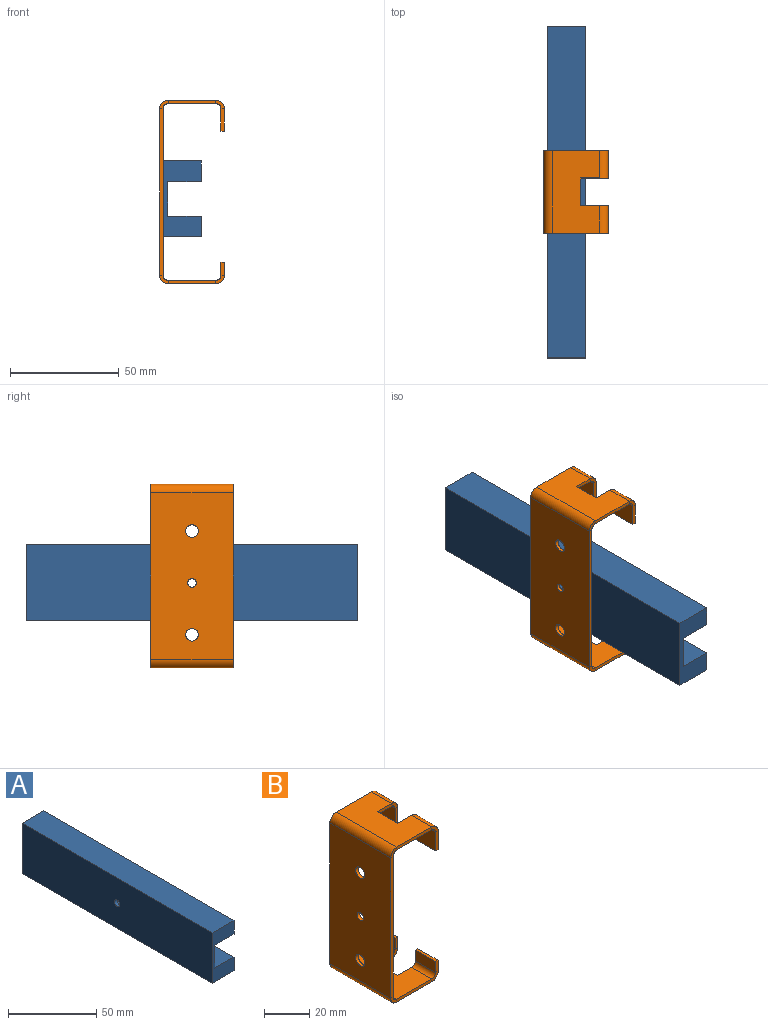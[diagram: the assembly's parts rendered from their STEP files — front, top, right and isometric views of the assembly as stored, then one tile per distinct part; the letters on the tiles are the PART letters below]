
ASSEMBLY  parts=2 mates=1
PART A: 11 faces, bbox 17.5x152.4x34.9 mm
  f0: plane 152.4x34.93mm, normal (-1,0,0), area 5306.7mm2, adj f1,f7,f8,f9,f10
  f1: plane 152.4x17.46mm, normal (0,0,-1), area 2661.3mm2, adj f0,f2,f8,f9
  f2: plane 152.4x9.53mm, normal (1,0,0), area 1451.6mm2, adj f1,f3,f8,f9
  f3: plane 152.4x15.24mm, normal (0,0,1), area 2322.6mm2, adj f2,f4,f8,f9
  f4: plane 152.4x15.88mm, normal (1,0,0), area 2403.5mm2, adj f3,f5,f8,f9,f10
  f5: plane 152.4x15.24mm, normal (0,0,-1), area 2322.6mm2, adj f4,f6,f8,f9
  f6: plane 152.4x9.53mm, normal (1,0,0), area 1451.6mm2, adj f5,f7,f8,f9
  f7: plane 152.4x17.46mm, normal (0,0,1), area 2661.3mm2, adj f0,f6,f8,f9
  f8: plane 34.93x17.46mm, normal (0,-1,0), area 367.9mm2, adj f0,f1,f2,f3,f4,f5,f6,f7
  f9: plane 34.93x17.46mm, normal (0,1,0), area 367.9mm2, adj f0,f1,f2,f3,f4,f5,f6,f7
  f10: cylinder r=2.25mm len=4.5mm, axis (1,0,0), area 31.4mm2, adj f0,f4
PART B: 65 faces, bbox 29.8x38.1x84.3 mm
  f0: plane 22.01x1.59mm, normal (0,-1,0), area 34.9mm2, adj f5,f6,f43,f61
  f1: plane 22.01x1.59mm, normal (0,1,0), area 34.9mm2, adj f5,f6,f44,f53
  f2: plane 8.83x1.59mm, normal (0,-1,0), area 14mm2, adj f3,f5,f6,f52
  f3: plane 12.7x1.59mm, normal (1,0,0), area 20.2mm2, adj f2,f4,f5,f6
  f4: plane 8.83x1.59mm, normal (0,1,0), area 14mm2, adj f3,f5,f6,f62
  f5: plane 38.1x22.01mm, normal (0,0,-1), area 726.5mm2, adj f0,f1,f2,f3,f4,f46,f55,f64
  f6: plane 38.1x22.01mm, normal (0,0,1), area 726.5mm2, adj f0,f1,f2,f3,f4,f45,f54,f63
  f7: plane 76.53x1.59mm, normal (0,1,0), area 121.5mm2, adj f12,f13,f40,f44
  f8: plane 76.53x1.59mm, normal (0,-1,0), area 121.5mm2, adj f12,f13,f39,f43
  f9: cylinder r=2.9mm len=5.79mm, axis (1,0,0), area 28.9mm2, adj f12,f13
  f10: cylinder r=2.9mm len=5.79mm, axis (1,0,0), area 28.9mm2, adj f12,f13
  f11: cylinder r=1.97mm len=3.94mm, axis (1,0,0), area 19.6mm2, adj f12,f13
  f12: plane 76.53x38.1mm, normal (1,0,0), area 2850.9mm2, adj f7,f8,f9,f10,f11,f42,f46
  f13: plane 76.53x38.1mm, normal (-1,0,0), area 2850.9mm2, adj f7,f8,f9,f10,f11,f41,f45
  f14: plane 22.01x1.59mm, normal (0,1,0), area 34.9mm2, adj f19,f20,f27,f40
  f15: plane 22.01x1.59mm, normal (0,-1,0), area 34.9mm2, adj f19,f20,f35,f39
  f16: plane 8.83x1.59mm, normal (0,1,0), area 14mm2, adj f17,f19,f20,f36
  f17: plane 12.7x1.59mm, normal (1,0,0), area 20.2mm2, adj f16,f18,f19,f20
  f18: plane 8.83x1.59mm, normal (0,-1,0), area 14mm2, adj f17,f19,f20,f26
  f19: plane 38.1x22.01mm, normal (0,0,1), area 726.5mm2, adj f14,f15,f16,f17,f18,f29,f38,f42
  f20: plane 38.1x22.01mm, normal (0,0,-1), area 726.5mm2, adj f14,f15,f16,f17,f18,f28,f37,f41
  f21: plane 12.7x1.59mm, normal (0,0,1), area 20.2mm2, adj f22,f23,f24,f25
  f22: plane 5.98x1.59mm, normal (0,1,0), area 9.5mm2, adj f21,f24,f25,f27
  f23: plane 5.98x1.59mm, normal (0,-1,0), area 9.5mm2, adj f21,f24,f25,f26
  f24: plane 12.7x5.98mm, normal (-1,0,0), area 76mm2, adj f21,f22,f23,f29
  f25: plane 12.7x5.98mm, normal (1,0,0), area 76mm2, adj f21,f22,f23,f28
  f26: plane 3.87x3.87mm, normal (0,-1,0), area 7.7mm2, adj f18,f23,f28,f29
  f27: plane 3.87x3.87mm, normal (0,1,0), area 7.7mm2, adj f14,f22,f28,f29
  f28: cylinder r=3.87mm len=12.7mm, axis (0,-1,0), area 77.3mm2, adj f20,f25,f26,f27
  f29: cylinder r=2.29mm len=12.7mm, axis (0,-1,0), area 45.6mm2, adj f19,f24,f26,f27
  f30: plane 5.98x1.59mm, normal (0,-1,0), area 9.5mm2, adj f31,f33,f34,f35
  f31: plane 12.7x1.59mm, normal (0,0,1), area 20.2mm2, adj f30,f32,f33,f34
  f32: plane 5.98x1.59mm, normal (0,1,0), area 9.5mm2, adj f31,f33,f34,f36
  f33: plane 12.7x5.98mm, normal (-1,0,0), area 76mm2, adj f30,f31,f32,f38
  f34: plane 12.7x5.98mm, normal (1,0,0), area 76mm2, adj f30,f31,f32,f37
  f35: plane 3.87x3.87mm, normal (0,-1,0), area 7.7mm2, adj f15,f30,f37,f38
  f36: plane 3.87x3.87mm, normal (0,1,0), area 7.7mm2, adj f16,f32,f37,f38
  f37: cylinder r=3.87mm len=12.7mm, axis (0,-1,0), area 77.3mm2, adj f20,f34,f35,f36
  f38: cylinder r=2.29mm len=12.7mm, axis (0,-1,0), area 45.6mm2, adj f19,f33,f35,f36
  f39: plane 3.87x3.87mm, normal (0,-1,0), area 7.7mm2, adj f8,f15,f41,f42
  f40: plane 3.87x3.87mm, normal (0,1,0), area 7.7mm2, adj f7,f14,f41,f42
  f41: cylinder r=3.87mm len=38.1mm, axis (0,-1,0), area 231.8mm2, adj f13,f20,f39,f40
  f42: cylinder r=2.29mm len=38.1mm, axis (0,-1,0), area 136.8mm2, adj f12,f19,f39,f40
  f43: plane 3.87x3.87mm, normal (0,-1,0), area 7.7mm2, adj f0,f8,f45,f46
  f44: plane 3.87x3.87mm, normal (0,1,0), area 7.7mm2, adj f1,f7,f45,f46
  f45: cylinder r=3.87mm len=38.1mm, axis (0,-1,0), area 231.8mm2, adj f6,f13,f43,f44
  f46: cylinder r=2.29mm len=38.1mm, axis (0,-1,0), area 136.8mm2, adj f5,f12,f43,f44
  f47: plane 10.35x1.59mm, normal (0,1,0), area 16.4mm2, adj f48,f50,f51,f53
  f48: plane 12.7x1.59mm, normal (0,0,-1), area 20.2mm2, adj f47,f49,f50,f51
  f49: plane 10.35x1.59mm, normal (0,-1,0), area 16.4mm2, adj f48,f50,f51,f52
  f50: plane 12.7x10.35mm, normal (-1,0,0), area 131.5mm2, adj f47,f48,f49,f55
  f51: plane 12.7x10.35mm, normal (1,0,0), area 131.5mm2, adj f47,f48,f49,f54
  f52: plane 3.87x3.87mm, normal (0,-1,0), area 7.7mm2, adj f2,f49,f54,f55
  f53: plane 3.87x3.87mm, normal (0,1,0), area 7.7mm2, adj f1,f47,f54,f55
  f54: cylinder r=3.87mm len=12.7mm, axis (0,-1,0), area 77.3mm2, adj f6,f51,f52,f53
  f55: cylinder r=2.29mm len=12.7mm, axis (0,-1,0), area 45.6mm2, adj f5,f50,f52,f53
  f56: plane 12.7x1.59mm, normal (0,0,-1), area 20.2mm2, adj f57,f58,f59,f60
  f57: plane 10.35x1.59mm, normal (0,-1,0), area 16.4mm2, adj f56,f59,f60,f61
  f58: plane 10.35x1.59mm, normal (0,1,0), area 16.4mm2, adj f56,f59,f60,f62
  f59: plane 12.7x10.35mm, normal (-1,0,0), area 131.5mm2, adj f56,f57,f58,f64
  f60: plane 12.7x10.35mm, normal (1,0,0), area 131.5mm2, adj f56,f57,f58,f63
  f61: plane 3.87x3.87mm, normal (0,-1,0), area 7.7mm2, adj f0,f57,f63,f64
  f62: plane 3.87x3.87mm, normal (0,1,0), area 7.7mm2, adj f4,f58,f63,f64
  f63: cylinder r=3.87mm len=12.7mm, axis (0,-1,0), area 77.3mm2, adj f6,f60,f61,f62
  f64: cylinder r=2.29mm len=12.7mm, axis (0,-1,0), area 45.6mm2, adj f5,f59,f61,f62
PLACE A t=(-34.86,0.35,-26.5)mm
PLACE B t=(-24.15,0.35,-19.93)mm fixed
MATE fastened A.f10 <-> B.f11  axis (-1,0,0) through (-52.32,0.35,-26.5)mm
